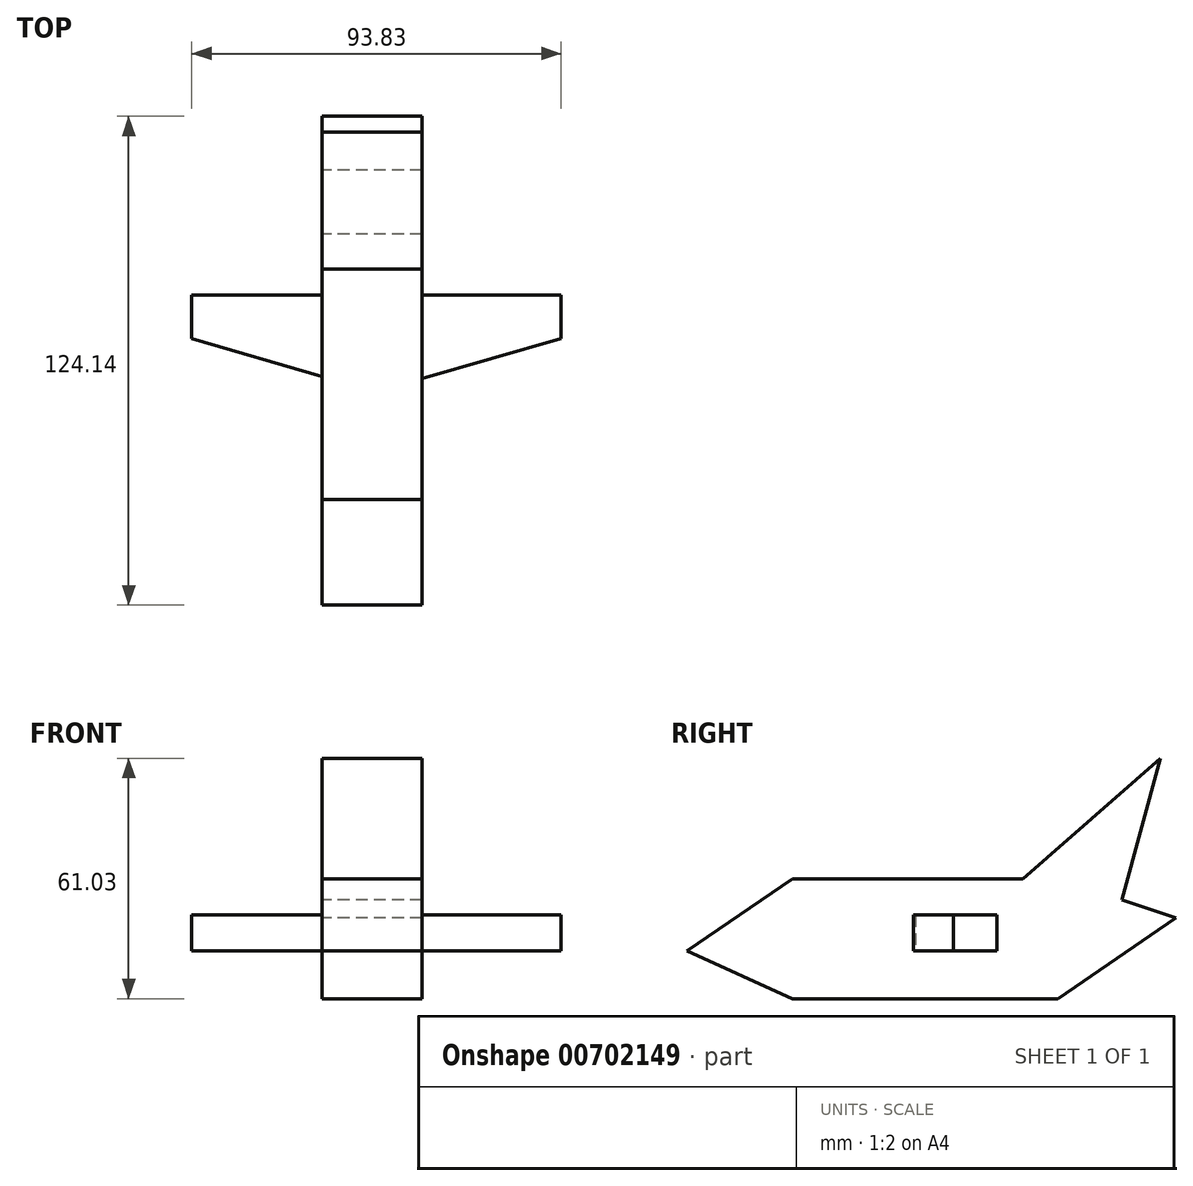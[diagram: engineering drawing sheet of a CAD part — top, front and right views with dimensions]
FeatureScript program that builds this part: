
annotation { "Feature Type Name" : "Feature", "Feature Type Description" : "" }
export const myFeature = defineFeature(function(context is Context, id is Id, definition is map)
    precondition{}
    {
        {
            var Q0;
            Q0=qCreatedBy(makeId("Right.planeOp"),FACE);
            var sketch = newSketch(context, id + "F0", { "sketchPlane" : qUnion([Q0])});
            skLineSegment(sketch, "E0", {"start": v(-54.1, 0) * mm, "end": v(-27.38, 18.34) * mm});
            skLineSegment(sketch, "E1", {"start": v(-27.38, 18.34) * mm, "end": v(40.1, 18.34) * mm});
            skLineSegment(sketch, "E2", {"start": v(-54.1, 0) * mm, "end": v(-27.38, -12.08) * mm});
            skLineSegment(sketch, "E3", {"start": v(-27.38, -12.08) * mm, "end": v(40.1, -12.08) * mm});
            skLineSegment(sketch, "E4", {"start": v(40.1, -12.08) * mm, "end": v(70.03, 8.47) * mm});
            skLineSegment(sketch, "E5", {"start": v(70.03, 8.47) * mm, "end": v(40.1, 18.34) * mm});
            skLineSegment(sketch, "E6", {"start": v(56.32, 13) * mm, "end": v(66.1, 48.95) * mm});
            skLineSegment(sketch, "E7", {"start": v(66.1, 48.95) * mm, "end": v(31.25, 18.34) * mm});
            skSolve(sketch);
        }
        {
            var Q0;
            Q0=qCreatedBy(makeId("Top.planeOp"),FACE);
            var sketch = newSketch(context, id + "F1", { "sketchPlane" : qUnion([Q0])});
            skLineSegment(sketch, "E8", {"start": v(13.55, 0) * mm, "end": v(60.74, 13.55) * mm});
            skLineSegment(sketch, "E9", {"start": v(60.74, 13.55) * mm, "end": v(60.74, 24.61) * mm});
            skLineSegment(sketch, "E10", {"start": v(60.74, 24.61) * mm, "end": v(17.97, 24.61) * mm});
            skLineSegment(sketch, "E11", {"start": v(17.97, 24.61) * mm, "end": v(-33.1, 24.61) * mm});
            skLineSegment(sketch, "E12", {"start": v(-33.1, 24.61) * mm, "end": v(-33.1, 13.55) * mm});
            skLineSegment(sketch, "E13", {"start": v(-33.1, 13.55) * mm, "end": v(13.55, 0) * mm});
            skSolve(sketch);
        }
        {
            var Q0;
            Q0 = qSketchRegion(id + "F1", true);
            extrude(context, id + "F2", {"entities" : qUnion([Q0]), "depth" : 9.14 * mm, "offsetDistance" : 25.4 * mm});
        }
        {
            var Q0;
            {var subQ4=sQuery(id+"F0.wireOp",EDGE,"E0");Q0=makeQuery(id+"F0.imprint","IMPRINT",FACE,{"disambiguationData":[TD([[makeQuery(id+"F0.imprint","IMPRINT",EDGE,{"derivedFrom":subQ4}),-1.0]])]});}
            var Q1;
            {var subQ4=sQuery(id+"F0.wireOp",EDGE,"E6");Q1=makeQuery(id+"F0.imprint","IMPRINT",FACE,{"disambiguationData":[TD([[makeQuery(id+"F0.imprint","IMPRINT",EDGE,{"derivedFrom":subQ4}),1.0]])]});}
            extrude(context, id + "F3", {"entities" : qUnion([Q0, Q1]), "operationType" : NewBodyOperationType.ADD, "depth" : 25.4 * mm, "offsetDistance" : 25.4 * mm});
        }
    });
